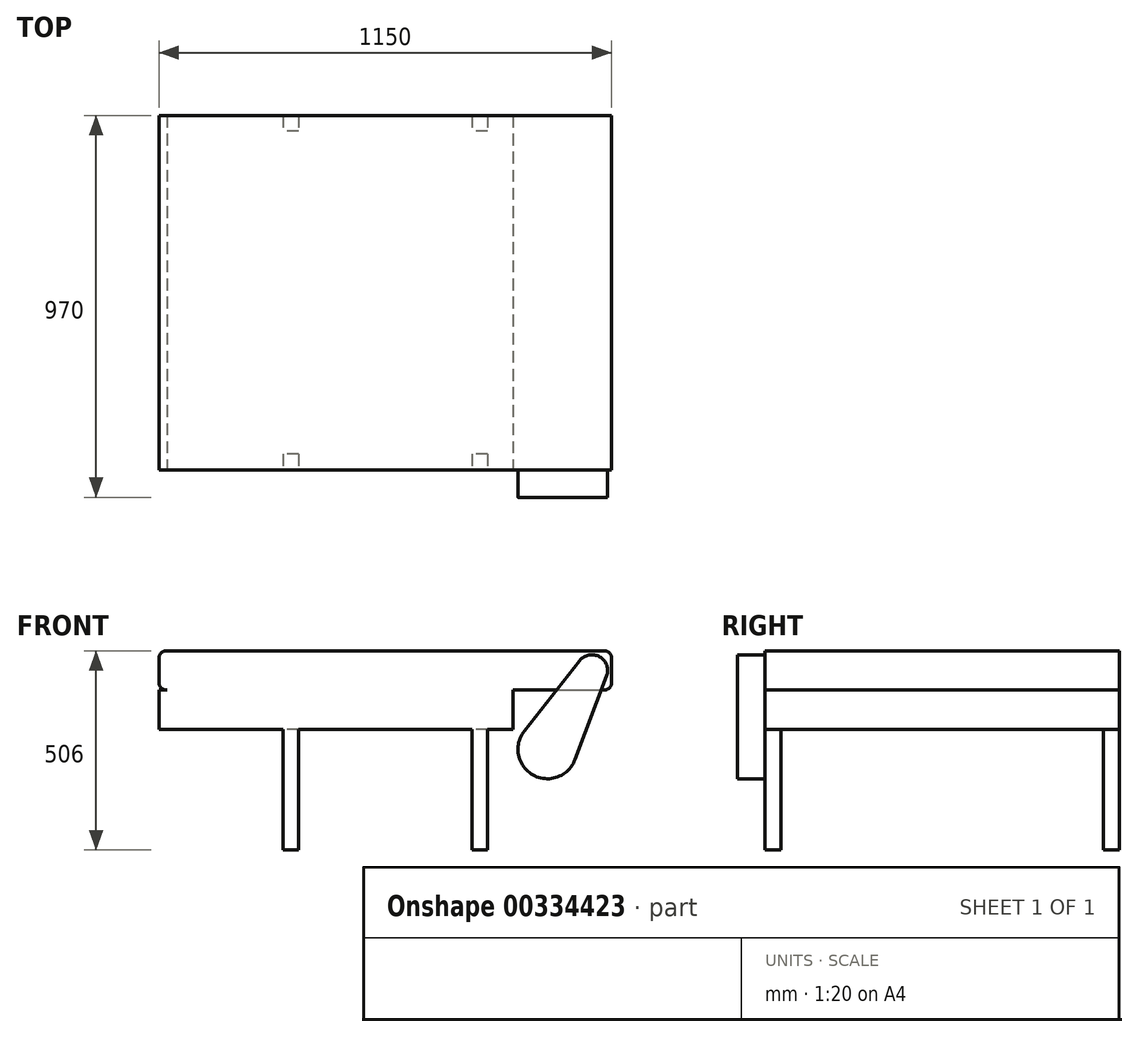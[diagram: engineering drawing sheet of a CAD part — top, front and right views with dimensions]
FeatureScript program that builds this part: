
annotation { "Feature Type Name" : "Feature", "Feature Type Description" : "" }
export const myFeature = defineFeature(function(context is Context, id is Id, definition is map)
    precondition{}
    {
        {
            var Q0;
            Q0=qCreatedBy(makeId("Front.planeOp"),FACE);
            var sketch = newSketch(context, id + "F0", { "sketchPlane" : qUnion([Q0])});
            skLineSegment(sketch, "E0.bottom", {"start": v(20, 0) * mm, "end": v(1130, 0) * mm});
            skLineSegment(sketch, "E0.top", {"start": v(20, 100) * mm, "end": v(1130, 100) * mm});
            skLineSegment(sketch, "E0.left", {"start": v(0, 20) * mm, "end": v(0, 80) * mm});
            skLineSegment(sketch, "E0.right", {"start": v(1150, 20) * mm, "end": v(1150, 80) * mm});
            skPoint(sketch, "E1.visualSharp", {"position": v(0, 100) * mm});
            skArc(sketch, "E1.filletArc", {"start": v(20, 100) * mm, "mid": v(5.86, 94.14) * mm, "end": v(0, 80) * mm});
            skPoint(sketch, "E2.visualSharp", {"position": v(0, 0) * mm});
            skArc(sketch, "E2.filletArc", {"start": v(0, 20) * mm, "mid": v(5.86, 5.86) * mm, "end": v(20, 0) * mm});
            skPoint(sketch, "E3.visualSharp", {"position": v(1150, 100) * mm});
            skArc(sketch, "E3.filletArc", {"start": v(1150, 80) * mm, "mid": v(1144.14, 94.14) * mm, "end": v(1130, 100) * mm});
            skPoint(sketch, "E4.visualSharp", {"position": v(1150, 0) * mm});
            skArc(sketch, "E4.filletArc", {"start": v(1130, 0) * mm, "mid": v(1144.14, 5.86) * mm, "end": v(1150, 20) * mm});
            skSolve(sketch);
        }
        {
            var Q0;
            Q0=makeQuery(id+"F0.imprint","IMPRINT",FACE,{"disambiguationData":[TD([[makeQuery(id+"F0.imprint","IMPRINT",EDGE,{"derivedFrom":sQuery(id+"F0.wireOp",EDGE,"E0.bottom")}),1.0]])]});
            extrude(context, id + "F1", {"entities" : qUnion([Q0]), "oppositeDirection" : true, "depth" : 900 * mm});
        }
        {
            var Q0;
            Q0=qCreatedBy(makeId("Front.planeOp"),FACE);
            var sketch = newSketch(context, id + "F2", { "sketchPlane" : qUnion([Q0])});
            skLineSegment(sketch, "E5.bottom", {"start": v(0, 0) * mm, "end": v(900, 0) * mm});
            skLineSegment(sketch, "E5.top", {"start": v(0, -100) * mm, "end": v(900, -100) * mm});
            skLineSegment(sketch, "E5.left", {"start": v(0, 0) * mm, "end": v(0, -100) * mm});
            skLineSegment(sketch, "E5.right", {"start": v(900, 0) * mm, "end": v(900, -100) * mm});
            skSolve(sketch);
        }
        {
            var Q0;
            Q0 = qSketchRegion(id + "F2", true);
            var Q1;
            Q1=makeQuery(id+"F1.opExtrude","CAP_FACE",FACE,{"disambiguationData":[OSD([sQuery(id+"F0.wireOp",EDGE,"E0.bottom"),sQuery(id+"F0.wireOp",EDGE,"E0.top"),sQuery(id+"F0.wireOp",EDGE,"E0.left"),sQuery(id+"F0.wireOp",EDGE,"E0.right"),sQuery(id+"F0.wireOp",EDGE,"E1.filletArc"),sQuery(id+"F0.wireOp",EDGE,"E2.filletArc"),sQuery(id+"F0.wireOp",EDGE,"E3.filletArc"),sQuery(id+"F0.wireOp",EDGE,"E4.filletArc")])],"isStart":false});
            extrude(context, id + "F3", {"entities" : qUnion([Q0]), "operationType" : NewBodyOperationType.ADD, "endBound" : BoundingType.UP_TO_SURFACE, "oppositeDirection" : true, "endBoundEntityFace" : qUnion([Q1]), "depth" : 25 * mm});
        }
        {
            var Q0;
            Q0=makeQuery(id+"F3.boolean.opBoolean","MERGE",FACE,{"derivedFrom":[makeQuery(id+"F1.opExtrude","CAP_FACE",FACE,{"disambiguationData":[OSD([sQuery(id+"F0.wireOp",EDGE,"E0.bottom"),sQuery(id+"F0.wireOp",EDGE,"E0.top"),sQuery(id+"F0.wireOp",EDGE,"E0.left"),sQuery(id+"F0.wireOp",EDGE,"E0.right"),sQuery(id+"F0.wireOp",EDGE,"E1.filletArc"),sQuery(id+"F0.wireOp",EDGE,"E2.filletArc"),sQuery(id+"F0.wireOp",EDGE,"E3.filletArc"),sQuery(id+"F0.wireOp",EDGE,"E4.filletArc")])],"isStart":true}),makeQuery(id+"F3.opExtrude","CAP_FACE",FACE,{"disambiguationData":[OSD([sQuery(id+"F2.wireOp",EDGE,"E5.bottom"),sQuery(id+"F2.wireOp",EDGE,"E5.top"),sQuery(id+"F2.wireOp",EDGE,"E5.left"),sQuery(id+"F2.wireOp",EDGE,"E5.right")])],"isStart":true})]});
            var sketch = newSketch(context, id + "F4", { "sketchPlane" : qUnion([Q0])});
            skCircle(sketch, "E6", {"center": v(1100, 50) * mm, "radius": 40 * mm});
            skPoint(sketch, "E6.centerSnap0", {"position": v(1150, 50) * mm});
            skCircle(sketch, "E7", {"center": v(987, -150) * mm, "radius": 75 * mm});
            skLineSegment(sketch, "E8", {"start": v(1057.16, -176.51) * mm, "end": v(1137.42, 35.86) * mm});
            skLineSegment(sketch, "E9", {"start": v(1100, 50) * mm, "end": v(987, -150) * mm, "construction": true});
            skLineSegment(sketch, "E10.MirrorCS", {"start": v(928.09, -103.59) * mm, "end": v(1068.58, 74.75) * mm});
            skSolve(sketch);
        }
        {
            var Q0;
            Q0 = qSketchRegion(id + "F4", true);
            extrude(context, id + "F5", {"entities" : qUnion([Q0]), "operationType" : NewBodyOperationType.ADD, "depth" : 70 * mm});
        }
        {
            var Q0;
            Q0=makeQuery(id+"F3.opExtrude","SWEPT_FACE",FACE,{"disambiguationData":[OSD([sQuery(id+"F2.wireOp",EDGE,"E5.top")])]});
            cPlane(context, id + "F6", {"entities" : qUnion([Q0]), "cplaneType" : CPlaneType.OFFSET, "offset" : 306 * mm, "width" : 150 * mm, "height" : 150 * mm});
        }
        {
            var Q0;
            Q0=qCreatedBy(id+"F6.planeOp",FACE);
            var sketch = newSketch(context, id + "F7", { "sketchPlane" : qUnion([Q0])});
            skLineSegment(sketch, "E11", {"start": v(-1252.8, -450) * mm, "end": v(1252.8, -450) * mm, "construction": true});
            skLineSegment(sketch, "E12.bottom", {"start": v(315, 0) * mm, "end": v(355, 0) * mm});
            skLineSegment(sketch, "E12.top", {"start": v(315, -40) * mm, "end": v(355, -40) * mm});
            skLineSegment(sketch, "E12.left", {"start": v(315, 0) * mm, "end": v(315, -40) * mm});
            skLineSegment(sketch, "E12.right", {"start": v(355, 0) * mm, "end": v(355, -40) * mm});
            skLineSegment(sketch, "E13.MirrorCS", {"start": v(2152.8, -450) * mm, "end": v(-352.8, -450) * mm, "construction": true});
            skLineSegment(sketch, "E14.0.1.0", {"start": v(355, -860) * mm, "end": v(355, -900) * mm});
            skLineSegment(sketch, "E14.0.1.1", {"start": v(315, -860) * mm, "end": v(315, -900) * mm});
            skLineSegment(sketch, "E14.0.1.2", {"start": v(315, -900) * mm, "end": v(355, -900) * mm});
            skLineSegment(sketch, "E14.0.1.3", {"start": v(315, -860) * mm, "end": v(355, -860) * mm});
            skLineSegment(sketch, "E14.1.0.0", {"start": v(835, 0) * mm, "end": v(835, -40) * mm});
            skLineSegment(sketch, "E14.1.0.1", {"start": v(795, 0) * mm, "end": v(795, -40) * mm});
            skLineSegment(sketch, "E14.1.0.2", {"start": v(795, -40) * mm, "end": v(835, -40) * mm});
            skLineSegment(sketch, "E14.1.0.3", {"start": v(795, 0) * mm, "end": v(835, 0) * mm});
            skLineSegment(sketch, "E14.1.1.0", {"start": v(835, -860) * mm, "end": v(835, -900) * mm});
            skLineSegment(sketch, "E14.1.1.1", {"start": v(795, -860) * mm, "end": v(795, -900) * mm});
            skLineSegment(sketch, "E14.1.1.2", {"start": v(795, -900) * mm, "end": v(835, -900) * mm});
            skLineSegment(sketch, "E14.1.1.3", {"start": v(795, -860) * mm, "end": v(835, -860) * mm});
            skLineSegment(sketch, "E14.direction1", {"start": v(315, -40) * mm, "end": v(795, -40) * mm, "construction": true});
            skLineSegment(sketch, "E14.direction2", {"start": v(315, -40) * mm, "end": v(315, -900) * mm, "construction": true});
            skSolve(sketch);
        }
        {
            var Q0;
            Q0 = qSketchRegion(id + "F7", true);
            var Q1;
            Q1=makeQuery(id+"F3.opExtrude","SWEPT_FACE",FACE,{"disambiguationData":[OSD([sQuery(id+"F2.wireOp",EDGE,"E5.top")])]});
            extrude(context, id + "F8", {"entities" : qUnion([Q0]), "operationType" : NewBodyOperationType.ADD, "endBound" : BoundingType.UP_TO_SURFACE, "oppositeDirection" : true, "endBoundEntityFace" : qUnion([Q1]), "depth" : 25 * mm});
        }
    });
